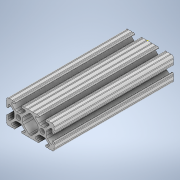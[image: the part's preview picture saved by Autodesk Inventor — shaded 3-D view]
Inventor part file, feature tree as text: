
AUTODESK INVENTOR PART (.ipt)
format: ipt  version: 2020 (Build 240168000, 168)  size: 333,824 bytes
history: native  units: in
note: dims shown in document units (in); Inventor stores cm internally (conversion verified against a paired STEP export)
features: sketch x2, extrude x1
ambient origin geometry x8: Origin, YZ Plane, XZ Plane, XY Plane, X Axis, Y Axis, Z Axis, Center Point
bodies: Solid1 (feature_tree)
feature tree (3):
  extrude  "Extrusion1"  [1 undecoded]
  sketch  "Sketch2"
  sketch  "Sketch1"  dims[d0=5.0in d1=0.0in]
note: 1 required parameter value undecoded (feature->parameter linkage not recoverable at this tier; creation-order binding heuristic only, values carry confidence <= 0.55)
